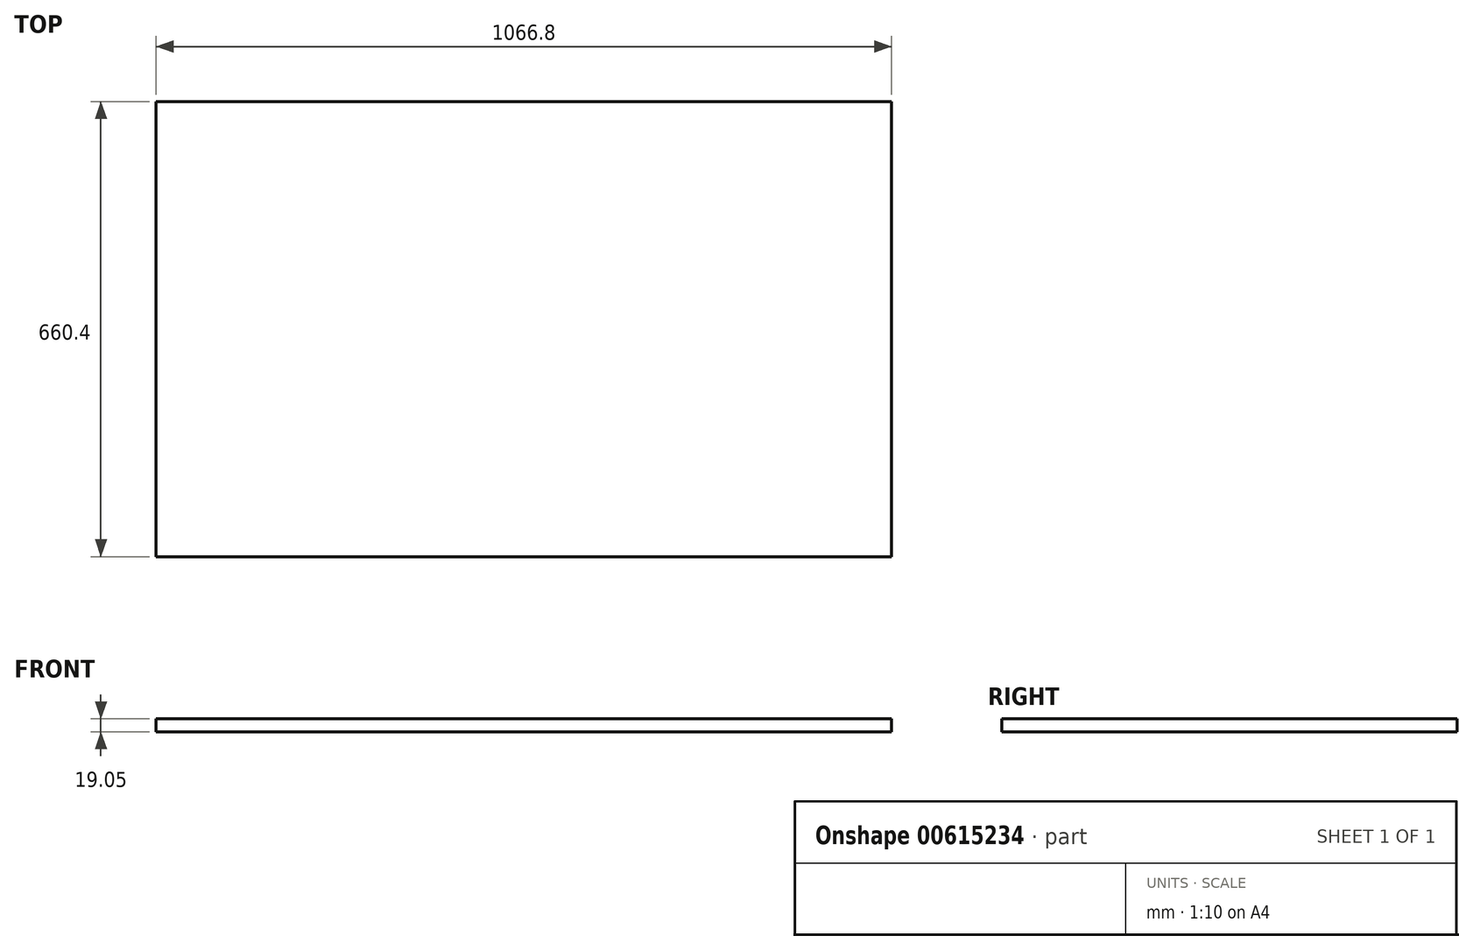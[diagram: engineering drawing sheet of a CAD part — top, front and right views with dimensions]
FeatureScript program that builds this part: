
annotation { "Feature Type Name" : "Feature", "Feature Type Description" : "" }
export const myFeature = defineFeature(function(context is Context, id is Id, definition is map)
    precondition{}
    {
        {
            var Q0;
            Q0=qCreatedBy(makeId("Top.planeOp"),FACE);
            var sketch = newSketch(context, id + "F0", { "sketchPlane" : qUnion([Q0])});
            skLineSegment(sketch, "E0.bottom", {"start": v(0, 0) * mm, "end": v(1066.8, 0) * mm});
            skLineSegment(sketch, "E0.top", {"start": v(0, 660.4) * mm, "end": v(1066.8, 660.4) * mm});
            skLineSegment(sketch, "E0.left", {"start": v(0, 0) * mm, "end": v(0, 660.4) * mm});
            skLineSegment(sketch, "E0.right", {"start": v(1066.8, 0) * mm, "end": v(1066.8, 660.4) * mm});
            skSolve(sketch);
        }
        {
            var Q0;
            Q0=makeQuery(id+"F0.imprint","IMPRINT",FACE,{"disambiguationData":[TD([[makeQuery(id+"F0.imprint","IMPRINT",EDGE,{"derivedFrom":sQuery(id+"F0.wireOp",EDGE,"E0.bottom")}),1.0]])]});
            extrude(context, id + "F1", {"entities" : qUnion([Q0]), "depth" : 19.05 * mm, "offsetDistance" : 25.4 * mm});
        }
    });
